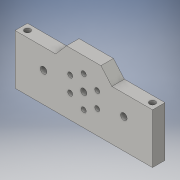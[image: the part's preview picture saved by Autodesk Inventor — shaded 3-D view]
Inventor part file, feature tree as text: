
AUTODESK INVENTOR PART (.ipt)
format: ipt  version: 2016 (Build 200138000, 138)  size: 369,152 bytes
history: native  units: mm
features: projected_geometry x8, extrude x5, other x4, sketch x3, fillet x2, hole x1
ambient origin geometry x8: Origin, YZ Plane, XZ Plane, XY Plane, X Axis, Y Axis, Z Axis, Center Point
bodies: Body1 (feature_tree)
feature tree (23):
  other  "構築線"
  extrude  "押し出し11"  Depth=17.0mm
  other  "固定穴"
  extrude  "押し出し19"  Depth=5.6mm
  extrude  "押し出し21"  Depth=10.0mm
  other  "ねじ穴+固定(基板)"
  hole  "ねじ穴(基板)"  [1 undecoded]
  extrude  "押し出し22"  Depth=10.0mm
  fillet  "フィレット1"  [1 undecoded]
  fillet  "フィレット2"  Radius=20.1mm
  extrude  "押し出し28"  TaperAngle=0.0deg  [1 undecoded]
  other  "外形上面(dxf出力用)"
  sketch  "スケッチ25"
  sketch  "スケッチ27"
  sketch  "スケッチ20"
  projected_geometry  "投影ループ4"
  projected_geometry  "投影ループ5"
  projected_geometry  "投影ループ6"
  projected_geometry  "投影ループ7"
  projected_geometry  "投影ループ8"
  projected_geometry  "投影ループ13"
  projected_geometry  "投影ループ14"
  projected_geometry  "投影ループ16"
note: 3 required parameter values undecoded (feature->parameter linkage not recoverable at this tier; creation-order binding heuristic only, values carry confidence <= 0.55)
